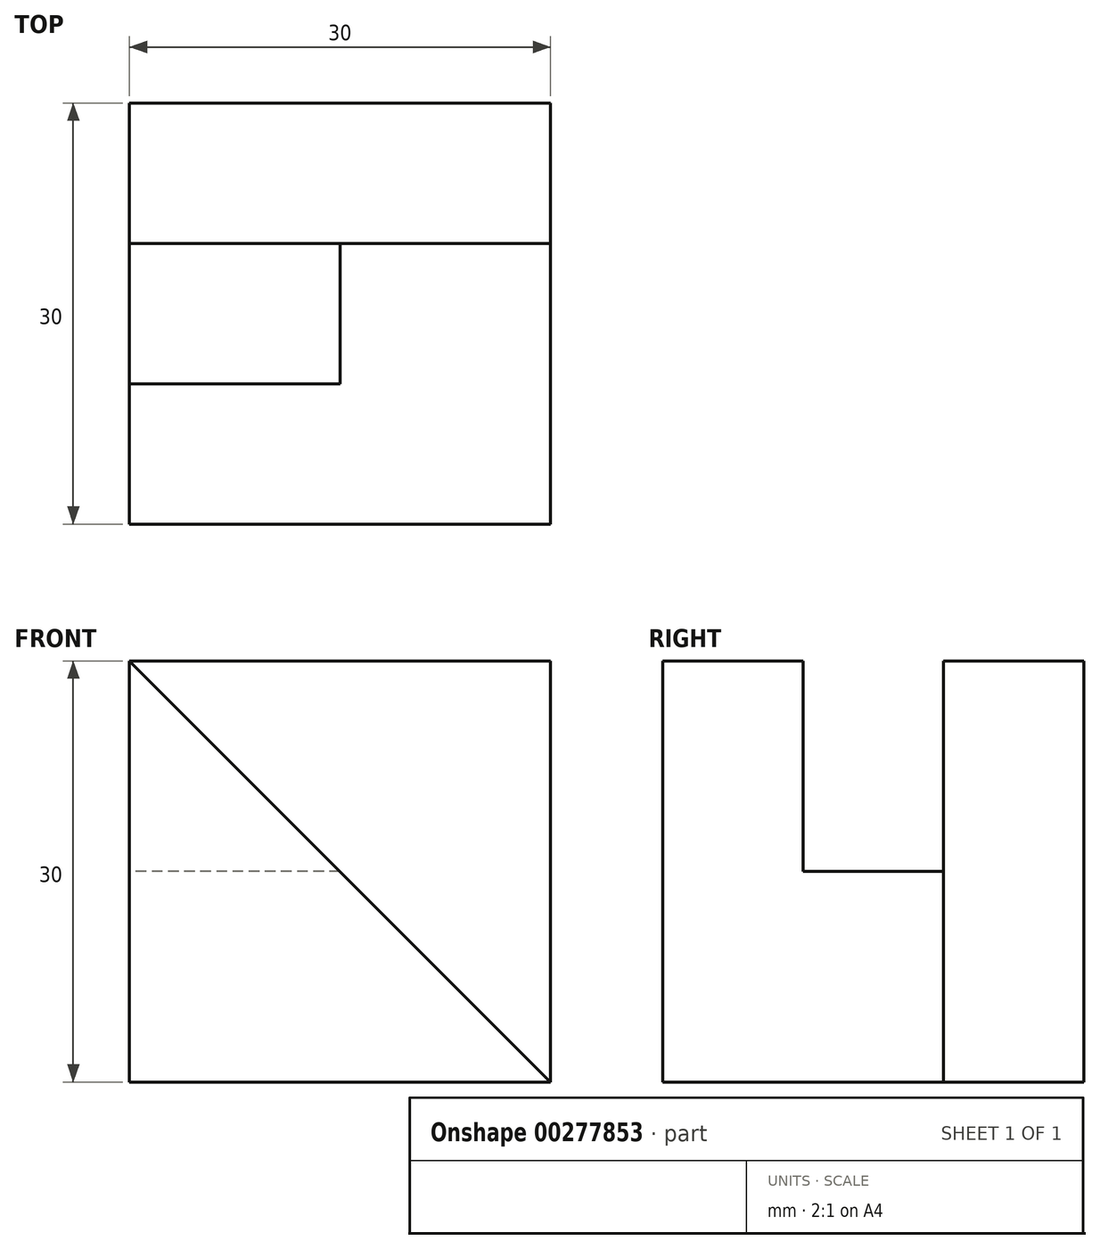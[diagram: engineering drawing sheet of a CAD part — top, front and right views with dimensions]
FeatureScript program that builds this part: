
annotation { "Feature Type Name" : "Feature", "Feature Type Description" : "" }
export const myFeature = defineFeature(function(context is Context, id is Id, definition is map)
    precondition{}
    {
        {
            var Q0;
            Q0=qCreatedBy(makeId("Front.planeOp"),FACE);
            var sketch = newSketch(context, id + "F0", { "sketchPlane" : qUnion([Q0])});
            skLineSegment(sketch, "E0.bottom", {"start": v(0, 0) * mm, "end": v(30, 0) * mm});
            skLineSegment(sketch, "E0.top", {"start": v(0, 30) * mm, "end": v(30, 30) * mm});
            skLineSegment(sketch, "E0.left", {"start": v(0, 0) * mm, "end": v(0, 30) * mm});
            skLineSegment(sketch, "E0.right", {"start": v(30, 0) * mm, "end": v(30, 30) * mm});
            skSolve(sketch);
        }
        {
            var Q0;
            Q0 = qSketchRegion(id + "F0", true);
            extrude(context, id + "F1", {"entities" : qUnion([Q0]), "depth" : 10 * mm});
        }
        {
            var Q0;
            Q0=makeQuery(id+"F1.opExtrude","CAP_FACE",FACE,{"disambiguationData":[OSD([sQuery(id+"F0.wireOp",EDGE,"E0.bottom"),sQuery(id+"F0.wireOp",EDGE,"E0.top"),sQuery(id+"F0.wireOp",EDGE,"E0.left"),sQuery(id+"F0.wireOp",EDGE,"E0.right")])],"isStart":false});
            var sketch = newSketch(context, id + "F2", { "sketchPlane" : qUnion([Q0])});
            skLineSegment(sketch, "E1.0", {"start": v(0, 0) * mm, "end": v(0, 30) * mm});
            skLineSegment(sketch, "E2.0", {"start": v(0, 0) * mm, "end": v(30, 0) * mm});
            skLineSegment(sketch, "E3", {"start": v(0, 30) * mm, "end": v(30, 0) * mm});
            skSolve(sketch);
        }
        {
            var Q0;
            Q0 = qSketchRegion(id + "F2", true);
            extrude(context, id + "F3", {"entities" : qUnion([Q0]), "operationType" : NewBodyOperationType.ADD, "depth" : 20 * mm});
        }
        {
            var Q0;
            Q0=makeQuery(id+"F3.boolean.opBoolean","MERGE",FACE,{"derivedFrom":[makeQuery(id+"F1.opExtrude","SWEPT_FACE",FACE,{"disambiguationData":[OSD([sQuery(id+"F0.wireOp",EDGE,"E0.left")])]}),makeQuery(id+"F3.opExtrude","SWEPT_FACE",FACE,{"disambiguationData":[OSD([sQuery(id+"F2.wireOp",EDGE,"E1.0")])]})]});
            var sketch = newSketch(context, id + "F4", { "sketchPlane" : qUnion([Q0])});
            skLineSegment(sketch, "E4", {"start": v(10, 30) * mm, "end": v(10, 15) * mm});
            skPoint(sketch, "E4.endSnap0", {"position": v(0, 15) * mm});
            skLineSegment(sketch, "E5", {"start": v(10, 15) * mm, "end": v(20, 15) * mm});
            skLineSegment(sketch, "E6", {"start": v(20, 15) * mm, "end": v(20, 30) * mm});
            skSolve(sketch);
        }
        {
            var Q0;
            Q0 = qSketchRegion(id + "F4", true);
            var Q1;
            {var subQ0=sQuery(id+"F4.wireOp",EDGE,"E4");Q1=makeQuery(id+"F4.imprint","IMPRINT",FACE,{"disambiguationData":[TD([[makeQuery(id+"F4.imprint","IMPRINT",EDGE,{"derivedFrom":subQ0}),1.0]])]});}
            extrude(context, id + "F5", {"entities" : qUnion([Q0, Q1]), "operationType" : NewBodyOperationType.REMOVE, "endBound" : BoundingType.THROUGH_ALL, "oppositeDirection" : true, "depth" : 25 * mm});
        }
    });
